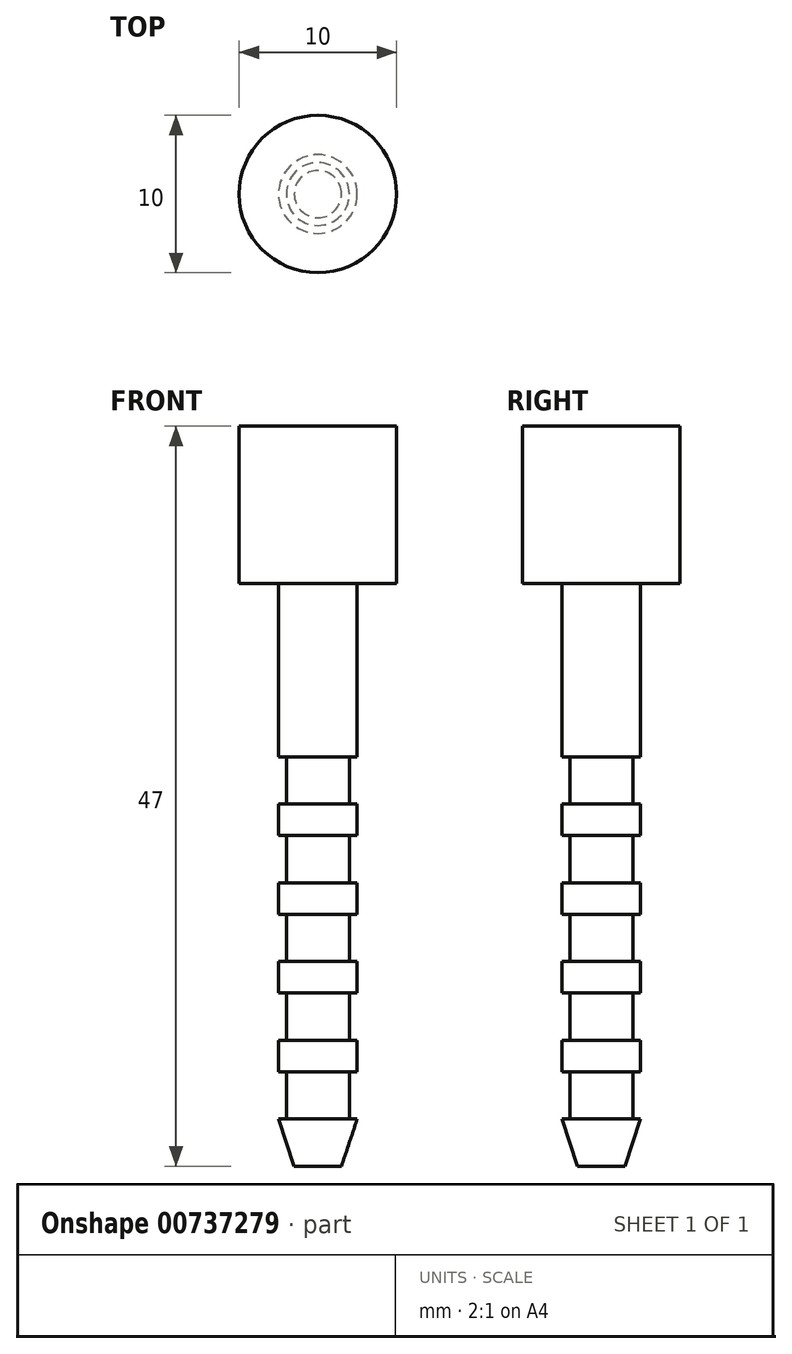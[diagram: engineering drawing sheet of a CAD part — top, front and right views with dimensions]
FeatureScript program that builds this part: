
annotation { "Feature Type Name" : "Feature", "Feature Type Description" : "" }
export const myFeature = defineFeature(function(context is Context, id is Id, definition is map)
    precondition{}
    {
        {
            var Q0;
            Q0=qCreatedBy(makeId("Front.planeOp"),FACE);
            var sketch = newSketch(context, id + "F0", { "sketchPlane" : qUnion([Q0])});
            skLineSegment(sketch, "E0", {"start": v(0, 28.86) * mm, "end": v(5, 28.86) * mm});
            skLineSegment(sketch, "E1", {"start": v(5, 28.86) * mm, "end": v(5, 18.86) * mm});
            skLineSegment(sketch, "E2", {"start": v(5, 18.86) * mm, "end": v(2.5, 18.86) * mm});
            skLineSegment(sketch, "E3", {"start": v(2, -2.14) * mm, "end": v(2.5, -2.14) * mm});
            skLineSegment(sketch, "E4", {"start": v(2, -2.14) * mm, "end": v(2, -5.14) * mm});
            skLineSegment(sketch, "E5", {"start": v(2.5, -5.14) * mm, "end": v(2, -5.14) * mm});
            skLineSegment(sketch, "E6", {"start": v(2.5, -5.14) * mm, "end": v(2.5, -7.14) * mm});
            skLineSegment(sketch, "E7", {"start": v(2, -7.14) * mm, "end": v(2.5, -7.14) * mm});
            skLineSegment(sketch, "E8", {"start": v(2, -7.14) * mm, "end": v(2, -10.14) * mm});
            skLineSegment(sketch, "E9", {"start": v(2.5, -10.14) * mm, "end": v(2, -10.14) * mm});
            skLineSegment(sketch, "E10", {"start": v(1.5, -18.14) * mm, "end": v(0, -18.14) * mm});
            skLineSegment(sketch, "E11", {"start": v(0, 28.86) * mm, "end": v(0, -18.14) * mm});
            skLineSegment(sketch, "E12", {"start": v(2.5, -10.14) * mm, "end": v(2.5, -12.14) * mm});
            skLineSegment(sketch, "E13", {"start": v(2, -12.14) * mm, "end": v(2.5, -12.14) * mm});
            skLineSegment(sketch, "E14", {"start": v(2, -12.14) * mm, "end": v(2, -15.14) * mm});
            skLineSegment(sketch, "E15", {"start": v(2.5, -15.14) * mm, "end": v(2, -15.14) * mm});
            skLineSegment(sketch, "E16", {"start": v(2.5, -15.14) * mm, "end": v(1.5, -18.14) * mm});
            skLineSegment(sketch, "E17", {"start": v(2, 2.86) * mm, "end": v(2.5, 2.86) * mm});
            skLineSegment(sketch, "E18", {"start": v(2.5, 2.86) * mm, "end": v(2.5, 4.86) * mm});
            skLineSegment(sketch, "E19", {"start": v(2.5, 4.86) * mm, "end": v(2, 4.86) * mm});
            skLineSegment(sketch, "E20", {"start": v(2, 4.86) * mm, "end": v(2, 7.86) * mm});
            skLineSegment(sketch, "E21", {"start": v(2, 7.86) * mm, "end": v(2.5, 7.86) * mm});
            skLineSegment(sketch, "E22", {"start": v(2.5, 18.86) * mm, "end": v(2.5, 7.86) * mm});
            skLineSegment(sketch, "E23", {"start": v(2.5, -0.14) * mm, "end": v(2.5, -2.14) * mm});
            skLineSegment(sketch, "E24", {"start": v(2, 2.86) * mm, "end": v(2, -0.14) * mm});
            skLineSegment(sketch, "E25", {"start": v(2, -0.14) * mm, "end": v(2.5, -0.14) * mm});
            skSolve(sketch);
        }
        {
            var Q0;
            Q0 = qSketchRegion(id + "F0", true);
            var Q1;
            Q1=sQuery(id+"F0.wireOp",EDGE,"E11");
            revolve(context, id + "F1", {"surfaceOperationType" : NewSurfaceOperationType.NEW, "entities" : qUnion([Q0]), "axis" : qUnion([Q1]), "revolveType" : RevolveType.FULL});
        }
    });
